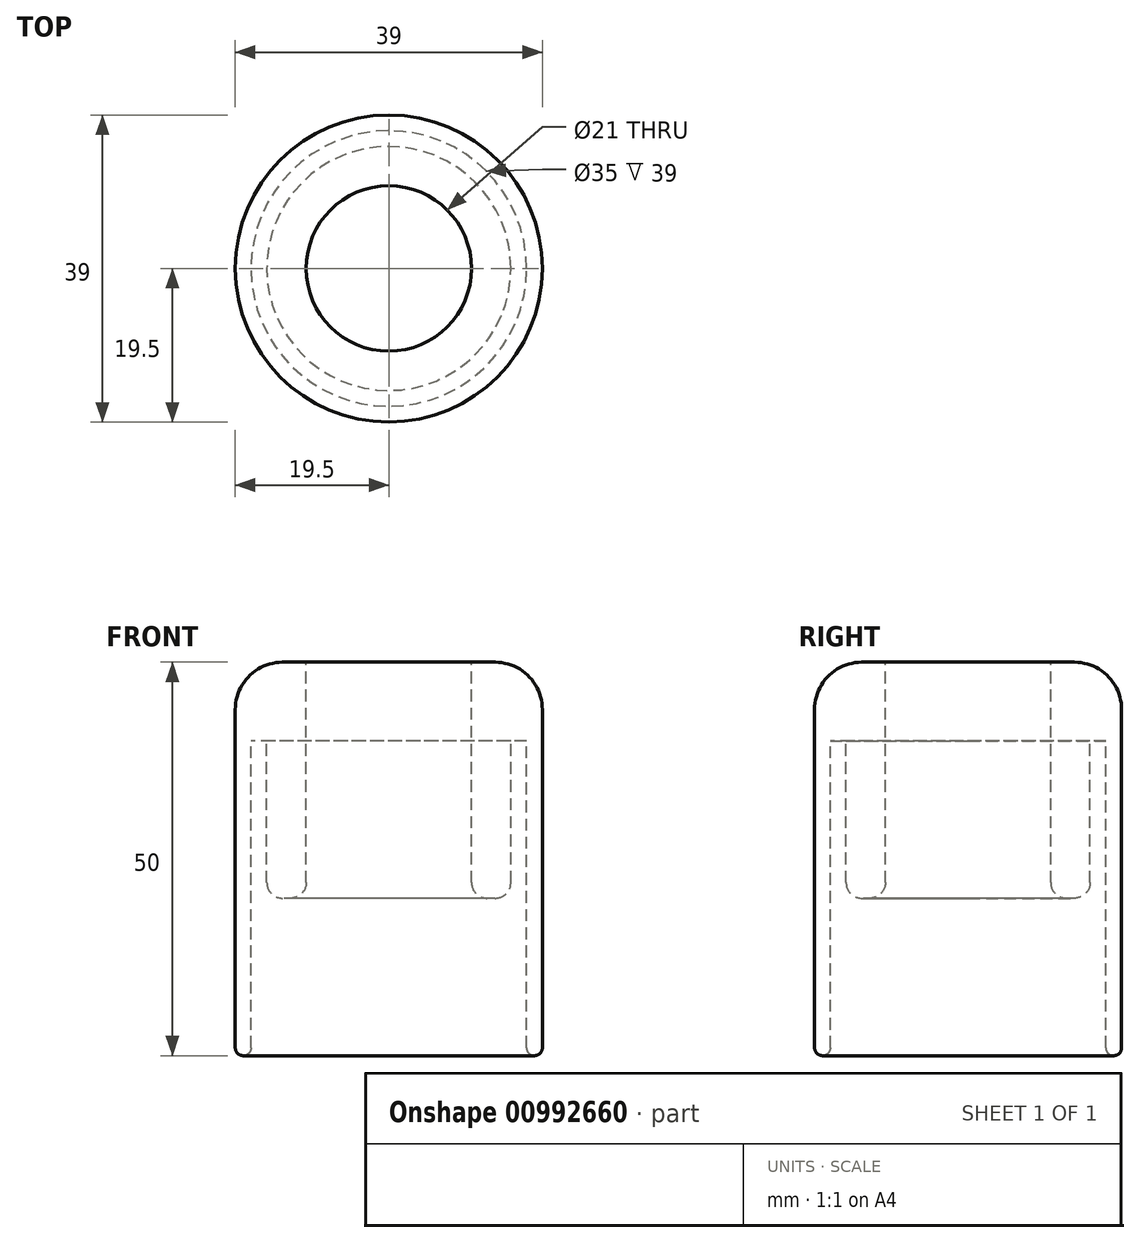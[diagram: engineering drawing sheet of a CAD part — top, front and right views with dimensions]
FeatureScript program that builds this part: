
annotation { "Feature Type Name" : "Feature", "Feature Type Description" : "" }
export const myFeature = defineFeature(function(context is Context, id is Id, definition is map)
    precondition{}
    {
        {
            var Q0;
            Q0=qCreatedBy(makeId("Front.planeOp"),FACE);
            var sketch = newSketch(context, id + "F0", { "sketchPlane" : qUnion([Q0])});
            skLineSegment(sketch, "E0", {"start": v(-10.5, 30) * mm, "end": v(-10.5, 0) * mm});
            skLineSegment(sketch, "E1", {"start": v(-10.5, 0) * mm, "end": v(-15.5, 0) * mm});
            skLineSegment(sketch, "E2", {"start": v(-15.5, 0) * mm, "end": v(-15.5, 20) * mm});
            skLineSegment(sketch, "E3", {"start": v(-15.5, 20) * mm, "end": v(-17.5, 20) * mm});
            skLineSegment(sketch, "E4", {"start": v(-17.5, 20) * mm, "end": v(-17.5, -20) * mm});
            skLineSegment(sketch, "E5", {"start": v(-17.5, -20) * mm, "end": v(-19.5, -20) * mm});
            skLineSegment(sketch, "E6", {"start": v(-19.5, -20) * mm, "end": v(-19.5, 20) * mm});
            skLineSegment(sketch, "E7", {"start": v(-19.5, 20) * mm, "end": v(-19.5, 23.98) * mm});
            skLineSegment(sketch, "E8", {"start": v(-13.53, 29.98) * mm, "end": v(-10.5, 30) * mm});
            skPoint(sketch, "E9.visualSharp", {"position": v(-19.5, 29.95) * mm});
            skArc(sketch, "E9.filletArc", {"start": v(-13.53, 29.98) * mm, "mid": v(-17.75, 28.22) * mm, "end": v(-19.5, 23.98) * mm});
            skLineSegment(sketch, "E10", {"start": v(0, 18.89) * mm, "end": v(0, 4.93) * mm});
            skSolve(sketch);
        }
        {
            var Q0;
            Q0=makeQuery(id+"F0.imprint","IMPRINT",FACE,{"disambiguationData":[TD([[makeQuery(id+"F0.imprint","IMPRINT",EDGE,{"derivedFrom":sQuery(id+"F0.wireOp",EDGE,"E0")}),-1.0]])]});
            var Q1;
            Q1=sQuery(id+"F0.wireOp",EDGE,"E10");
            revolve(context, id + "F1", {"surfaceOperationType" : NewSurfaceOperationType.NEW, "entities" : qUnion([Q0]), "axis" : qUnion([Q1]), "revolveType" : RevolveType.FULL});
        }
        {
            var Q0;
            Q0=makeQuery(id+"F1.opRevolve","SWEPT_EDGE",EDGE,{"disambiguationData":[OSD([sQuery(id+"F0.wireOp",EDGE,"E4"),sQuery(id+"F0.wireOp",EDGE,"E5")])]});
            var Q1;
            Q1=makeQuery(id+"F1.opRevolve","SWEPT_EDGE",EDGE,{"disambiguationData":[OSD([sQuery(id+"F0.wireOp",EDGE,"E5"),sQuery(id+"F0.wireOp",EDGE,"E6")])]});
            fillet(context, id + "F2", {"entities" : qUnion([Q0, Q1]), "radius" : 1 * mm, "tangentPropagation" : true, "allowEdgeOverflow" : false});
        }
        {
            var Q0;
            Q0=makeQuery(id+"F1.opRevolve","SWEPT_EDGE",EDGE,{"disambiguationData":[OSD([sQuery(id+"F0.wireOp",EDGE,"E0"),sQuery(id+"F0.wireOp",EDGE,"E1")])]});
            var Q1;
            Q1=makeQuery(id+"F1.opRevolve","SWEPT_EDGE",EDGE,{"disambiguationData":[OSD([sQuery(id+"F0.wireOp",EDGE,"E1"),sQuery(id+"F0.wireOp",EDGE,"E2")])]});
            fillet(context, id + "F3", {"entities" : qUnion([Q0, Q1]), "radius" : 2 * mm, "tangentPropagation" : true, "allowEdgeOverflow" : false});
        }
    });
